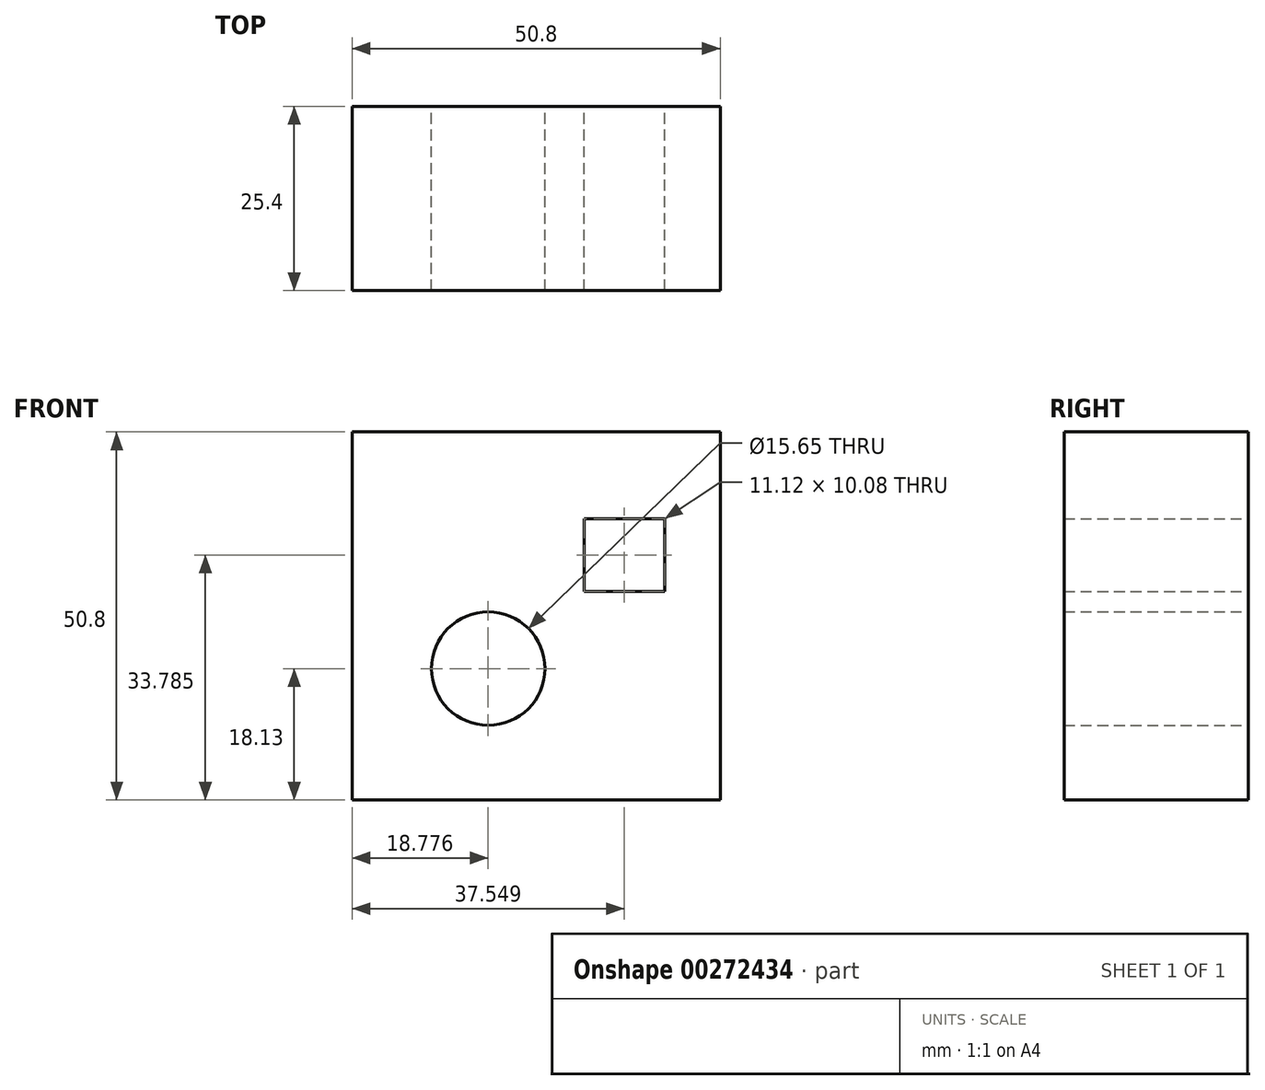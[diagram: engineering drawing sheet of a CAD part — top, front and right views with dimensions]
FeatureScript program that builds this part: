
annotation { "Feature Type Name" : "Feature", "Feature Type Description" : "" }
export const myFeature = defineFeature(function(context is Context, id is Id, definition is map)
    precondition{}
    {
        {
            var Q0;
            Q0=qCreatedBy(makeId("Front.planeOp"),FACE);
            var sketch = newSketch(context, id + "F0", { "sketchPlane" : qUnion([Q0])});
            skLineSegment(sketch, "E0.bottom", {"start": v(-25.27, 36.92) * mm, "end": v(25.53, 36.92) * mm});
            skLineSegment(sketch, "E0.top", {"start": v(-25.27, -13.88) * mm, "end": v(25.53, -13.88) * mm});
            skLineSegment(sketch, "E0.left", {"start": v(-25.27, 36.92) * mm, "end": v(-25.27, -13.88) * mm});
            skLineSegment(sketch, "E0.right", {"start": v(25.53, 36.92) * mm, "end": v(25.53, -13.88) * mm});
            skCircle(sketch, "E1", {"center": v(-6.5, 4.25) * mm, "radius": 7.82 * mm});
            skLineSegment(sketch, "E2.bottom", {"start": v(6.72, 24.95) * mm, "end": v(17.84, 24.95) * mm});
            skLineSegment(sketch, "E2.top", {"start": v(6.72, 14.86) * mm, "end": v(17.84, 14.86) * mm});
            skLineSegment(sketch, "E2.left", {"start": v(6.72, 24.95) * mm, "end": v(6.72, 14.86) * mm});
            skLineSegment(sketch, "E2.right", {"start": v(17.84, 24.95) * mm, "end": v(17.84, 14.86) * mm});
            skSolve(sketch);
        }
        {
            var Q0;
            Q0=makeQuery(id+"F0.imprint","IMPRINT",FACE,{"disambiguationData":[TD([[makeQuery(id+"F0.imprint","IMPRINT",EDGE,{"derivedFrom":sQuery(id+"F0.wireOp",EDGE,"E0.bottom")}),-1.0]])]});
            extrude(context, id + "F1", {"entities" : qUnion([Q0]), "depth" : 25.4 * mm});
        }
    });
